# Revit family: PRD_AR_JntrlUnits_SiriusMultiPurposeSink_BS353
name_source: partatom
category: Plumbing Fixtures
revit_build: Autodesk Revit 2018 (Build: 20190510_1515(x64)
units: mm (PartAtom-declared; Revit-internal decimal feet)

## family parameters
Always vertical = Yes
Cut with Voids When Loaded = No
OmniClass Number = 23.45.05.14.14
OmniClass Title = Sinks/Lavatories
Part Type = Normal
Room Calculation Point = No
Round Connector Dimension = Use Diameter
Shared = No
Work Plane-Based = No

## types (1)
- BS353
    AssetType = Fixed
    BIMObjectName = PRD_AR_JanitorialUnits_SiriusMultiPurposeSink_BS353
    Category = Pr_40_20_96_44, Janitorial sinks
    Color = Stainless steel
    Description = General purpose sink for inset or wall mounting, 2 bowls, stainless steel, surface satin finished, material thickness 1.2 mm, deep drawn seamless welded bowl, 1 1/2'' waste with standpipe strainer, drain board with riffle, 40 mm rear upstand, wall mounting brackets optional. two bowls (centric), two drain boards, width 2200 mm
    DrainSize = DN 40 (1 1/2 inch.)
    DurationUnit = year
    Features = stainless steel, 1.20 mm, satin finished, various types, 2200x357x550 mm (WxHxD)
    Finish = Satin finished
    FinishAndMaterial = Stainless steel 1.4301
    Form = Stainless steel multi purpose sink
    GrossWeight = 47.00 kg
    IfcExportAs = IfcSanitaryTerminalType
    IfcExportType = SINK
    Manufacturer = KWC Group AG
    ManufacturerName = KWC Group AG
    ManufacturerURL = www.kwc.com
    Material = Stainless steel
    Model = BS353
    ModelNumber = 2000100064
    ModelReference = BS353
    NBSDescription = Janitorial units
    NBSReference = 45-35-70/401
    Name = Sirius multi purpose sink BS353
    NetWeight = 24.00 kg
    NominalDepth = 550 mm  [stored 1.80446 ft]
    NominalHeight = 357 mm  [stored 1.17126 ft]
    NominalWidth = 2200 mm
    ProductInformation = https://pim.kwc.com
    Shape = Rectangular
    SinkMaterial = PRD_AR_StainlessSteel_SatinFinished
    SinkMounting = Other
    SinkType = Other
    Size = 2200 x 550 x 357 mm
    URL = www.kwc.com
    Uniclass2015Code = Pr_40_20_96_44
    Uniclass2015Title = Janitorial sinks
    Uniclass2015Version = Products v1.10
    Version = 1
    WarrantyDurationUnit = year
    WasteSize = 40  [stored 0.131234 ft]
    WaterSupplyOverflowAndWasteHolesOverflow = Stand pipe overflow
    WaterSupplyOverflowAndWasteHolesWaste = Center-Back
    WaterSupplyOverflowAndWasteHolesWaterSupply = No tapholes

note: [stored X ft] marks values corroborated as IEEE doubles in the binary element streams (Revit-internal decimal feet)

## geometry (parser evidence)
native form markers: Sweep x8
no freeform markers — native parametric forms only
